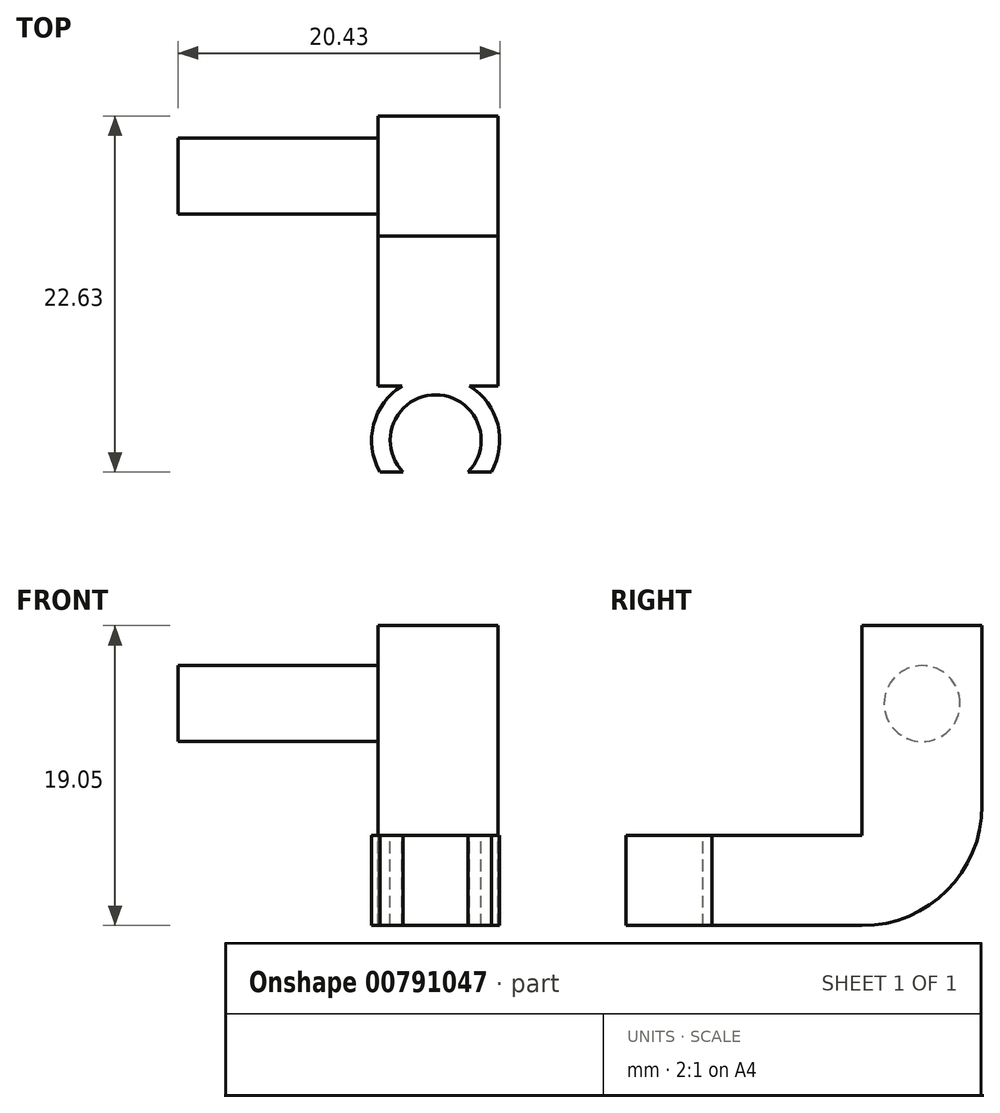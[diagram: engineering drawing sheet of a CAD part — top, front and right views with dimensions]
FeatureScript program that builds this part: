
annotation { "Feature Type Name" : "Feature", "Feature Type Description" : "" }
export const myFeature = defineFeature(function(context is Context, id is Id, definition is map)
    precondition{}
    {
        {
            var Q0;
            Q0=qCreatedBy(makeId("Front.planeOp"),FACE);
            var sketch = newSketch(context, id + "F0", { "sketchPlane" : qUnion([Q0])});
            skLineSegment(sketch, "E0.bottom", {"start": v(0, 26.58) * mm, "end": v(5.08, 26.58) * mm});
            skLineSegment(sketch, "E0.top", {"start": v(0, 13.88) * mm, "end": v(5.08, 13.88) * mm});
            skLineSegment(sketch, "E0.left", {"start": v(0, 26.58) * mm, "end": v(0, 13.88) * mm});
            skLineSegment(sketch, "E0.right", {"start": v(5.08, 26.58) * mm, "end": v(5.08, 13.88) * mm});
            skSolve(sketch);
        }
        {
            var Q0;
            Q0=qSketchRegion(id+"F0",true);
            extrude(context, id + "F1", {"entities" : qUnion([Q0]), "depth" : 5.08 * mm, "offsetDistance" : 25.4 * mm});
        }
        {
            var Q0;
            Q0=makeQuery(id+"F1.opExtrude","CAP_FACE",FACE,{"disambiguationData":[OSD([sQuery(id+"F0.wireOp",EDGE,"E0.bottom"),sQuery(id+"F0.wireOp",EDGE,"E0.top"),sQuery(id+"F0.wireOp",EDGE,"E0.left"),sQuery(id+"F0.wireOp",EDGE,"E0.right")])],"isStart":false});
            var sketch = newSketch(context, id + "F2", { "sketchPlane" : qUnion([Q0])});
            skLineSegment(sketch, "E1.bottom", {"start": v(0, 13.88) * mm, "end": v(5.08, 13.88) * mm});
            skLineSegment(sketch, "E1.top", {"start": v(0, 17.69) * mm, "end": v(5.08, 17.69) * mm});
            skLineSegment(sketch, "E1.left", {"start": v(0, 13.88) * mm, "end": v(0, 17.69) * mm});
            skLineSegment(sketch, "E1.right", {"start": v(5.08, 13.88) * mm, "end": v(5.08, 17.69) * mm});
            skSolve(sketch);
        }
        {
            var Q0;
            Q0=qSketchRegion(id+"F2",true);
            extrude(context, id + "F3", {"entities" : qUnion([Q0]), "operationType" : NewBodyOperationType.ADD, "depth" : 6.35 * mm, "offsetDistance" : 25.4 * mm});
        }
        {
            var Q0;
            Q0=makeQuery(id+"F1.opExtrude","CAP_EDGE",EDGE,{"disambiguationData":[OSD([sQuery(id+"F0.wireOp",EDGE,"E0.top")])],"isStart":true});
            fillet(context, id + "F4", {"entities" : qUnion([Q0]), "radius" : 5.08 * mm, "tangentPropagation" : true, "allowEdgeOverflow" : false});
        }
        {
            var Q0;
            Q0=makeQuery(id+"F3.opExtrude","SWEPT_FACE",FACE,{"disambiguationData":[OSD([sQuery(id+"F2.wireOp",EDGE,"E1.top")])]});
            var sketch = newSketch(context, id + "F5", { "sketchPlane" : qUnion([Q0])});
            skCircle(sketch, "E2", {"center": v(2.44, -13.74) * mm, "radius": 2.71 * mm});
            skPoint(sketch, "E2.first.point", {"position": v(2.54, -11.03) * mm});
            skPoint(sketch, "E2.first.point.positionSnap0", {"position": v(2.54, -11.43) * mm});
            skPoint(sketch, "E2.second.point", {"position": v(2.1, -16.43) * mm});
            skPoint(sketch, "E2.third.point", {"position": v(3.02, -16.39) * mm});
            skSolve(sketch);
        }
        {
            var Q0;
            Q0=qSketchRegion(id+"F5",true);
            extrude(context, id + "F6", {"entities" : qUnion([Q0]), "operationType" : NewBodyOperationType.ADD, "oppositeDirection" : true, "depth" : 3.8 * mm, "offsetDistance" : 25.4 * mm});
        }
        {
            var Q0;
            Q0=makeQuery(id+"F6.boolean.opBoolean","MERGE",FACE,{"derivedFrom":[makeQuery(id+"F3.opExtrude","SWEPT_FACE",FACE,{"disambiguationData":[OSD([sQuery(id+"F2.wireOp",EDGE,"E1.top")])]}),makeQuery(id+"F6.opExtrude","CAP_FACE",FACE,{"disambiguationData":[OSD([sQuery(id+"F5.wireOp",EDGE,"E2")])],"isStart":true})]});
            var sketch = newSketch(context, id + "F7", { "sketchPlane" : qUnion([Q0])});
            skCircle(sketch, "E3", {"center": v(2.44, -13.74) * mm, "radius": 1.93 * mm});
            skSolve(sketch);
        }
        {
            var Q0;
            Q0=qSketchRegion(id+"F7",true);
            extrude(context, id + "F8", {"entities" : qUnion([Q0]), "operationType" : NewBodyOperationType.REMOVE, "oppositeDirection" : true, "depth" : 3.8 * mm, "offsetDistance" : 25.4 * mm});
        }
        {
            var Q0;
            Q0=makeQuery(id+"F6.boolean.opBoolean","MERGE",FACE,{"derivedFrom":[makeQuery(id+"F3.opExtrude","SWEPT_FACE",FACE,{"disambiguationData":[OSD([sQuery(id+"F2.wireOp",EDGE,"E1.top")])]}),makeQuery(id+"F6.opExtrude","CAP_FACE",FACE,{"disambiguationData":[OSD([sQuery(id+"F5.wireOp",EDGE,"E2")])],"isStart":true})]});
            var sketch = newSketch(context, id + "F9", { "sketchPlane" : qUnion([Q0])});
            skLineSegment(sketch, "E4.bottom", {"start": v(0.08, -15.08) * mm, "end": v(5.44, -15.08) * mm});
            skLineSegment(sketch, "E4.top", {"start": v(0.08, -16.71) * mm, "end": v(5.44, -16.71) * mm});
            skLineSegment(sketch, "E4.left", {"start": v(0.08, -15.08) * mm, "end": v(0.08, -16.71) * mm});
            skLineSegment(sketch, "E4.right", {"start": v(5.44, -15.08) * mm, "end": v(5.44, -16.71) * mm});
            skSolve(sketch);
        }
        {
            var Q0;
            Q0=qSketchRegion(id+"F9",true);
            extrude(context, id + "F10", {"entities" : qUnion([Q0]), "operationType" : NewBodyOperationType.REMOVE, "oppositeDirection" : true, "depth" : 3.8 * mm, "offsetDistance" : 25.4 * mm});
        }
        {
            var Q0;
            Q0=makeQuery(id+"F1.opExtrude","SWEPT_BODY",BODY,{"disambiguationData":[OSD([sQuery(id+"F0.wireOp",EDGE,"E0.bottom"),sQuery(id+"F0.wireOp",EDGE,"E0.top"),sQuery(id+"F0.wireOp",EDGE,"E0.left"),sQuery(id+"F0.wireOp",EDGE,"E0.right")])]});
            var Q1;
            Q1=qCreatedBy(makeId("Origin.pointOp"),VERTEX);
            transform(context, id + "F11", {"entities" : qUnion([Q0]), "transformType" : TransformType.SCALE_UNIFORMLY, "scale" : 1.5, "scalePoint" : qUnion([Q1]), "makeCopy" : false});
        }
        {
            var Q0;
            Q0=makeQuery(id+"F3.boolean.opBoolean","MERGE",FACE,{"derivedFrom":[makeQuery(id+"F1.opExtrude","SWEPT_FACE",FACE,{"disambiguationData":[OSD([sQuery(id+"F0.wireOp",EDGE,"E0.right")])]}),makeQuery(id+"F3.opExtrude","SWEPT_FACE",FACE,{"disambiguationData":[OSD([sQuery(id+"F2.wireOp",EDGE,"E1.right")])]})]});
            var sketch = newSketch(context, id + "F12", { "sketchPlane" : qUnion([Q0])});
            skCircle(sketch, "E5", {"center": v(-3.81, 34.92) * mm, "radius": 2.41 * mm});
            skPoint(sketch, "E5.centerSnap0", {"position": v(-3.81, 39.87) * mm});
            skSolve(sketch);
        }
        {
            var Q0;
            Q0=makeQuery(id+"F12.imprint","IMPRINT",FACE,{"disambiguationData":[TD([[makeQuery(id+"F12.imprint","IMPRINT",EDGE,{"derivedFrom":sQuery(id+"F12.wireOp",EDGE,"E5")}),1.0]])]});
            extrude(context, id + "F13", {"entities" : qUnion([Q0]), "operationType" : NewBodyOperationType.ADD, "oppositeDirection" : true, "depth" : 20.32 * mm, "offsetDistance" : 25.4 * mm});
        }
    });
